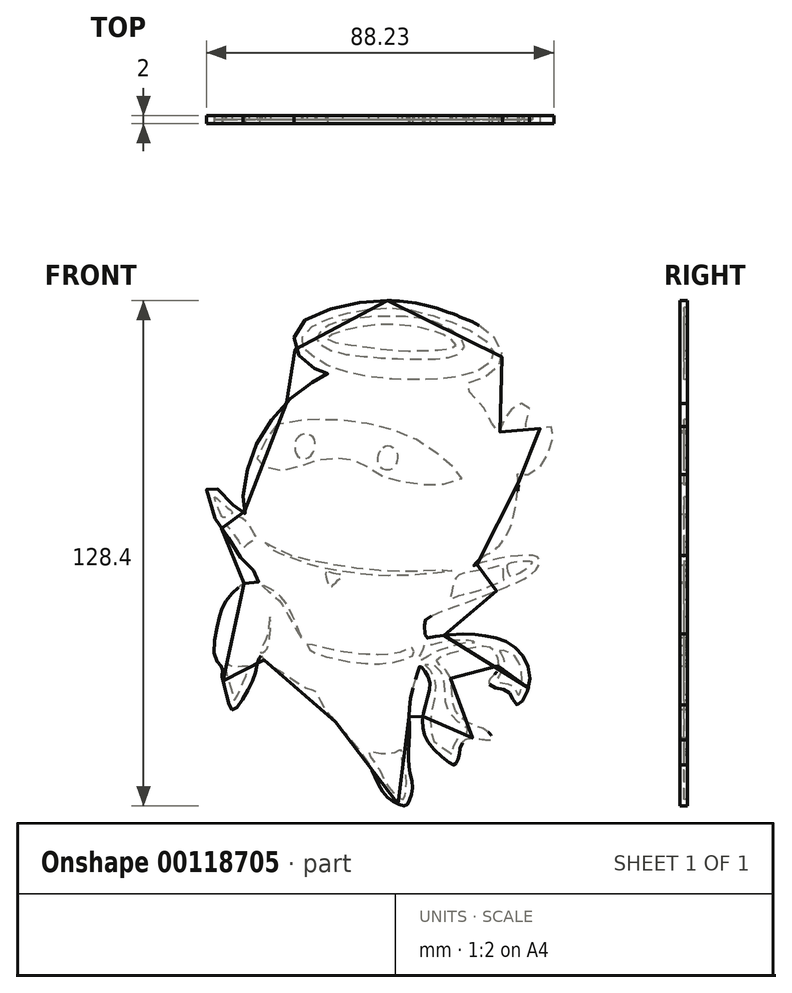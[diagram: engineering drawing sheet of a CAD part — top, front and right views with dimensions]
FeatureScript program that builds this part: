
annotation { "Feature Type Name" : "Feature", "Feature Type Description" : "" }
export const myFeature = defineFeature(function(context is Context, id is Id, definition is map)
    precondition{}
    {
        {
            var Q0;
            Q0=qCreatedBy(makeId("Front.planeOp"),FACE);
            var sketch = newSketch(context, id + "F0", { "sketchPlane" : qUnion([Q0])});
            skFitSpline(sketch, "E0", {"points": [v(2.08, 54.07) * mm, v(-5.17, 53.57) * mm, v(-13.1, 51.71) * mm, v(-19.17, 48.85) * mm, v(-21.36, 45.64) * mm, v(-21.53, 42.1) * mm, v(-19.68, 39.4) * mm, v(-16.64, 36.87) * mm, v(-13.94, 35.86) * mm, v(-13.1, 35.52) * mm, v(-13.6, 35.36) * mm, v(-16.98, 33.33) * mm, v(-22.04, 29.62) * mm, v(-27.1, 24.06) * mm, v(-31.14, 17.82) * mm, v(-33.33, 11.58) * mm, v(-34.52, 4.83) * mm, v(-34.52, 1.3) * mm, v(-34.18, -0.22) * mm, v(-35.02, 0.11) * mm, v(-38.23, 3.32) * mm, v(-41.26, 6.35) * mm, v(-43.45, 7.53) * mm, v(-43.28, 2.47) * mm, v(-39.74, -4.27) * mm, v(-37.55, -7.48) * mm, v(-34.85, -11.7) * mm, v(-33, -13.55) * mm, v(-30.64, -15.74) * mm, v(-30.47, -16.58) * mm, v(-30.97, -17.76) * mm, v(-33.17, -17.6) * mm, v(-35.36, -18.44) * mm, v(-39.07, -22.48) * mm, v(-40.92, -27.54) * mm, v(-41.6, -36.99) * mm, v(-39.91, -39) * mm, v(-39.91, -40.86) * mm, v(-38.73, -46.43) * mm, v(-37.21, -49.97) * mm, v(-34.18, -46.43) * mm, v(-31.48, -40.36) * mm, v(-30.64, -36.99) * mm, v(-30.13, -36.14) * mm, v(-29.12, -37.5) * mm, v(-24.73, -40.36) * mm, v(-18.66, -44.24) * mm, v(-16.13, -45.25) * mm, v(-15.63, -46.26) * mm, v(-13.94, -49.46) * mm, v(-12.09, -51.82) * mm, v(-9.39, -55.03) * mm, v(-6.19, -58.9) * mm, v(-3.15, -62.95) * mm, v(-1.3, -66.33) * mm, v(1.23, -71.22) * mm, v(4.6, -73.75) * mm, v(6.8, -74.25) * mm, v(7.64, -72.9) * mm, v(8.48, -69.7) * mm, v(7.64, -65.15) * mm, v(7.47, -60.26) * mm, v(7.64, -53.85) * mm, v(7.98, -46.77) * mm, v(10, -39.68) * mm, v(10.34, -38.84) * mm, v(11.69, -40.19) * mm, v(12.87, -43.56) * mm, v(11.69, -48.79) * mm, v(11.01, -54.02) * mm, v(12.87, -58.74) * mm, v(18.6, -63.8) * mm, v(19.28, -63.8) * mm, v(20.12, -62.28) * mm, v(20.63, -59.41) * mm, v(22.48, -57.22) * mm, v(27.2, -57.56) * mm, v(28.55, -57.22) * mm, v(27.7, -55.53) * mm, v(23.83, -53.68) * mm, v(19.61, -50.64) * mm, v(18.43, -44.74) * mm, v(17.25, -40.19) * mm, v(14.56, -37.32) * mm, v(18.77, -35.3) * mm, v(24.17, -33.95) * mm, v(28.21, -33.95) * mm, v(30.07, -36.82) * mm, v(29.73, -40.36) * mm, v(28.05, -42.21) * mm, v(28.05, -43.56) * mm, v(30.57, -44.57) * mm, v(32.77, -45.25) * mm, v(33.95, -47.27) * mm, v(35.13, -48.62) * mm, v(37.32, -46.1) * mm, v(38, -39.52) * mm, v(34.96, -34.46) * mm, v(30.57, -31.93) * mm, v(25.68, -30.92) * mm, v(19.28, -30.75) * mm, v(12.53, -31.59) * mm, v(11.86, -31.59) * mm, v(11.52, -28.9) * mm, v(11.69, -27.2) * mm, v(13.54, -25.86) * mm, v(21.97, -22.65) * mm, v(33.95, -17.93) * mm, v(40.02, -14.22) * mm, v(40.7, -11.52) * mm, v(38.84, -10.68) * mm, v(31.08, -11.35) * mm, v(24.5, -13.04) * mm, v(24, -13.2) * mm, v(26.7, -10.68) * mm, v(28.38, -10) * mm, v(30.74, -7.81) * mm, v(33.44, -3.1) * mm, v(35.13, 5.34) * mm, v(35.3, 9.72) * mm, v(35.13, 10.06) * mm, v(38.16, 9.9) * mm, v(41.54, 12.76) * mm, v(43.73, 17.48) * mm, v(44.23, 21.53) * mm, v(43.22, 22.03) * mm, v(39.34, 21.2) * mm, v(36.81, 21.2) * mm, v(37.32, 22.88) * mm, v(38, 27.1) * mm, v(36.3, 27.94) * mm, v(33.95, 26.76) * mm, v(31.92, 24.4) * mm, v(30.4, 20.52) * mm, v(29.06, 22.03) * mm, v(26.36, 27.1) * mm, v(21.97, 32.49) * mm, v(24.84, 33.84) * mm, v(30.4, 37.55) * mm, v(31.08, 41.26) * mm, v(27.7, 46.15) * mm, v(19.95, 50.2) * mm, v(11.01, 53.06) * mm, v(2.08, 54.07) * mm]});
            skFitSpline(sketch, "E1", {"points": [v(-25.98, 22.59) * mm, v(-28.54, 19.18) * mm, v(-31.1, 13.4) * mm, v(-30.24, 12.46) * mm, v(-26.55, 11.04) * mm, v(-21.54, 11.52) * mm, v(-16.9, 13.31) * mm, v(-10.84, 14.07) * mm, v(-7.53, 13.88) * mm, v(-3.55, 12.27) * mm, v(-0.34, 10) * mm, v(5.34, 8.2) * mm, v(12.44, 7.26) * mm, v(17.27, 7.64) * mm, v(21.24, 9.24) * mm, v(18.78, 11.7) * mm, v(13.3, 16.34) * mm, v(4.68, 20.8) * mm, v(-4.5, 23.06) * mm, v(-12.64, 23.82) * mm, v(-17.47, 23.72) * mm, v(-25.98, 22.59) * mm]});
            skFitSpline(sketch, "E2", {"points": [v(-19.08, 20.13) * mm, v(-20.78, 19.18) * mm, v(-21.35, 17.95) * mm, v(-21.35, 15.68) * mm, v(-20.3, 14.26) * mm, v(-18.6, 13.98) * mm, v(-16.8, 15.5) * mm, v(-16.33, 17.95) * mm, v(-17, 19.56) * mm, v(-19.08, 20.13) * mm]});
            skFitSpline(sketch, "E3", {"points": [v(0.99, 16.72) * mm, v(2.12, 17.29) * mm, v(3.64, 16.72) * mm, v(4.58, 15.3) * mm, v(4.49, 13.4) * mm, v(3.64, 11.52) * mm, v(2.12, 11.04) * mm, v(0.14, 11.8) * mm, v(-0.34, 13.7) * mm, v(0.04, 15.5) * mm, v(0.99, 16.72) * mm]});
            skFitSpline(sketch, "E4", {"points": [v(-19.36, 42.1) * mm, v(-19.68, 44.24) * mm, v(-18, 46.87) * mm, v(-12.36, 49.65) * mm, v(-5.83, 51.32) * mm, v(2.2, 52.28) * mm, v(11.6, 50.85) * mm, v(19, 48.38) * mm, v(25.53, 45.04) * mm, v(28.7, 41.85) * mm, v(28.95, 40.1) * mm, v(27.67, 37.64) * mm, v(21.39, 35.01) * mm, v(14.38, 34.14) * mm, v(4.52, 34.06) * mm, v(-4.95, 35.17) * mm, v(-13.55, 37.8) * mm, v(-17.93, 40.74) * mm, v(-19.36, 42.1) * mm]});
            skFitSpline(sketch, "E5", {"points": [v(-14.66, 42.8) * mm, v(-11.32, 41.06) * mm, v(-2.96, 39.79) * mm, v(4.91, 39.3) * mm, v(14.78, 39.3) * mm, v(18.84, 39.94) * mm, v(21.23, 41.38) * mm, v(21.55, 43.53) * mm, v(18.52, 46.4) * mm, v(12.63, 49.18) * mm, v(4.6, 50.05) * mm, v(-4.24, 49.81) * mm, v(-9.97, 48.86) * mm, v(-13.55, 47.43) * mm, v(-15.78, 44.96) * mm, v(-15.86, 44.08) * mm, v(-14.66, 42.8) * mm]});
            skFitSpline(sketch, "E6", {"points": [v(-13.15, 44.32) * mm, v(-5.2, 42.57) * mm, v(4.36, 41.38) * mm, v(14.54, 41.54) * mm, v(19.48, 42.57) * mm, v(18.2, 44.32) * mm, v(13.59, 46.4) * mm, v(6.98, 47.74) * mm, v(0.22, 47.98) * mm, v(-5.35, 47.27) * mm, v(-11.32, 45.75) * mm, v(-13.15, 44.32) * mm]});
            skFitSpline(sketch, "E7", {"points": [v(-39.65, -1.04) * mm, v(-40.69, 0.87) * mm, v(-41.8, 4.13) * mm, v(-39.17, 1.9) * mm, v(-37.34, 0.31) * mm, v(-38.23, -0.56) * mm, v(-39.65, -1.04) * mm]});
            skFitSpline(sketch, "E8", {"points": [v(-34.4, -8.68) * mm, v(-33.2, -7.49) * mm, v(-31.14, -6.45) * mm, v(-31.53, -5.58) * mm, v(-32.89, -3.27) * mm, v(-35.83, -0.88) * mm, v(-37.42, -2.15) * mm, v(-38.94, -2.71) * mm, v(-37.42, -4.54) * mm, v(-34.4, -8.68) * mm]});
            skFitSpline(sketch, "E9", {"points": [v(-13.55, -14.89) * mm, v(-12.67, -18.7) * mm, v(-12.28, -18.7) * mm, v(-9.65, -16.16) * mm, v(-9.33, -15.68) * mm, v(-11.96, -15.13) * mm, v(-13.55, -14.89) * mm]});
            skFitSpline(sketch, "E10", {"points": [v(-28.99, -7.33) * mm, v(-25.49, -9.32) * mm, v(-15.78, -12.18) * mm, v(-2.09, -14.25) * mm, v(10, -14.57) * mm, v(18.2, -14.4) * mm, v(18.52, -14.57) * mm, v(15.18, -15.05) * mm, v(6.74, -15.76) * mm, v(-1.13, -15.68) * mm, v(-8.46, -14.89) * mm, v(-15.38, -13.61) * mm, v(-20.95, -11.86) * mm, v(-25.8, -9.95) * mm, v(-27.95, -8.68) * mm, v(-28.99, -7.33) * mm]});
            skFitSpline(sketch, "E11", {"points": [v(21.63, -15.13) * mm, v(19.48, -16.32) * mm, v(18.52, -19.18) * mm, v(18.04, -21.5) * mm, v(17.97, -21.97) * mm, v(20.11, -20.86) * mm, v(23.14, -20.22) * mm, v(31.65, -16.88) * mm, v(31.65, -16.64) * mm, v(31.26, -13.22) * mm, v(29.82, -13.53) * mm, v(21.63, -15.13) * mm]});
            skFitSpline(sketch, "E12", {"points": [v(32.45, -13.22) * mm, v(33, -15.6) * mm, v(33.64, -16) * mm, v(37.94, -13.53) * mm, v(38.9, -12.42) * mm, v(38.18, -12.18) * mm, v(34.6, -12.42) * mm, v(32.45, -13.22) * mm]});
            skFitSpline(sketch, "E13", {"points": [v(-29.78, -18.3) * mm, v(-26.44, -21.17) * mm, v(-23.18, -25.71) * mm, v(-19.84, -31.76) * mm, v(-19.52, -32.24) * mm, v(-21.75, -26.59) * mm, v(-26.28, -19.98) * mm, v(-29.78, -18.3) * mm]});
            skFitSpline(sketch, "E14", {"points": [v(-39.1, -38.36) * mm, v(-37.1, -46.56) * mm, v(-36.79, -47.44) * mm, v(-33.29, -39.8) * mm, v(-33.29, -38.92) * mm, v(-36.3, -39) * mm, v(-38.06, -38.6) * mm, v(-39.1, -38.36) * mm]});
            skFitSpline(sketch, "E15", {"points": [v(-18.32, -33.35) * mm, v(-17.29, -34.86) * mm, v(-13.79, -36.3) * mm, v(-6.07, -37.89) * mm, v(2.77, -37.97) * mm, v(8.26, -36.3) * mm, v(8.73, -35.42) * mm, v(8.65, -34.3) * mm, v(7.38, -34.38) * mm, v(5.55, -35.26) * mm, v(0.14, -35.9) * mm, v(-6.47, -35.58) * mm, v(-11.96, -34.62) * mm, v(-17.13, -33.35) * mm, v(-18.32, -33.35) * mm]});
            skFitSpline(sketch, "E16", {"points": [v(11.36, -33.59) * mm, v(10.88, -35.02) * mm, v(9.93, -36.77) * mm, v(10.17, -37.33) * mm, v(13.75, -35.42) * mm, v(17.97, -33.9) * mm, v(22.18, -32.8) * mm, v(24.1, -32.8) * mm, v(24.33, -32.63) * mm, v(22.42, -32.32) * mm, v(17.33, -32.47) * mm, v(12.4, -33.5) * mm, v(11.36, -33.59) * mm]});
            skFitSpline(sketch, "E17", {"points": [v(-27.8, -26.35) * mm, v(-28.2, -29.85) * mm, v(-28.99, -32.32) * mm, v(-30.13, -35.34) * mm, v(-29.07, -35.02) * mm, v(-27.95, -32.47) * mm, v(-27.64, -27.54) * mm, v(-27.8, -26.35) * mm]});
            skFitSpline(sketch, "E18", {"points": [v(11.68, -38.44) * mm, v(12.63, -39.56) * mm, v(13.9, -41.63) * mm, v(14.3, -44.57) * mm, v(13.43, -49.9) * mm, v(12.95, -53.17) * mm, v(13.67, -57.46) * mm, v(14.94, -58.82) * mm, v(17.8, -60.73) * mm, v(18.44, -61.44) * mm, v(18.84, -59.45) * mm, v(19.88, -57.14) * mm, v(22.5, -55.71) * mm, v(22.58, -54.92) * mm, v(19.16, -52.3) * mm, v(16.93, -48.4) * mm, v(16.61, -43.7) * mm, v(16.13, -41.23) * mm, v(14.15, -38.6) * mm, v(11.68, -38.44) * mm]});
            skFitSpline(sketch, "E19", {"points": [v(30.54, -34.94) * mm, v(31.33, -36.21) * mm, v(31.26, -39.8) * mm, v(29.82, -42.34) * mm, v(30.3, -42.82) * mm, v(32.85, -43.38) * mm, v(34.6, -44.73) * mm, v(35.31, -46.16) * mm, v(35.71, -45.69) * mm, v(36.27, -41.87) * mm, v(35.71, -38.6) * mm, v(33.4, -35.5) * mm, v(30.54, -34.94) * mm]});
            skFitSpline(sketch, "E20", {"points": [v(-2.65, -60.73) * mm, v(-0.66, -63.99) * mm, v(1.01, -67.17) * mm, v(3.56, -71) * mm, v(5.95, -72.66) * mm, v(6.66, -71) * mm, v(6.82, -66.85) * mm, v(5.79, -63.11) * mm, v(5.55, -60) * mm, v(4.28, -60.65) * mm, v(0.7, -61.12) * mm, v(-2.65, -60.73) * mm]});
            skSolve(sketch);
        }
        {
            var Q0;
            Q0=makeQuery(id+"F0.imprint","IMPRINT",FACE,{"disambiguationData":[TD([[makeQuery(id+"F0.imprint","IMPRINT",EDGE,{"derivedFrom":sQuery(id+"F0.wireOp",EDGE,"E5")}),1.0]])]});
            var Q1;
            Q1=makeQuery(id+"F0.imprint","IMPRINT",FACE,{"disambiguationData":[TD([[makeQuery(id+"F0.imprint","IMPRINT",EDGE,{"derivedFrom":sQuery(id+"F0.wireOp",EDGE,"E0")}),1.0]])]});
            var Q2;
            Q2=makeQuery(id+"F0.imprint","IMPRINT",FACE,{"disambiguationData":[TD([[makeQuery(id+"F0.imprint","IMPRINT",EDGE,{"derivedFrom":sQuery(id+"F0.wireOp",EDGE,"E2")}),1.0]])]});
            var Q3;
            Q3=makeQuery(id+"F0.imprint","IMPRINT",FACE,{"disambiguationData":[TD([[makeQuery(id+"F0.imprint","IMPRINT",EDGE,{"derivedFrom":sQuery(id+"F0.wireOp",EDGE,"E3")}),-1.0]])]});
            extrude(context, id + "F1", {"entities" : qUnion([Q0, Q1, Q2, Q3]), "oppositeDirection" : true, "depth" : 1 * mm});
        }
        {
            var Q0;
            Q0=makeQuery(id+"F0.imprint","IMPRINT",FACE,{"disambiguationData":[TD([[makeQuery(id+"F0.imprint","IMPRINT",EDGE,{"derivedFrom":sQuery(id+"F0.wireOp",EDGE,"E4")}),-1.0]])]});
            var Q1;
            Q1=makeQuery(id+"F0.imprint","IMPRINT",FACE,{"disambiguationData":[TD([[makeQuery(id+"F0.imprint","IMPRINT",EDGE,{"derivedFrom":sQuery(id+"F0.wireOp",EDGE,"E15")}),1.0]])]});
            var Q2;
            Q2=makeQuery(id+"F0.imprint","IMPRINT",FACE,{"disambiguationData":[TD([[makeQuery(id+"F0.imprint","IMPRINT",EDGE,{"derivedFrom":sQuery(id+"F0.wireOp",EDGE,"E11")}),1.0]])]});
            var Q3;
            Q3=makeQuery(id+"F0.imprint","IMPRINT",FACE,{"disambiguationData":[TD([[makeQuery(id+"F0.imprint","IMPRINT",EDGE,{"derivedFrom":sQuery(id+"F0.wireOp",EDGE,"E6")}),1.0]])]});
            var Q4;
            Q4=makeQuery(id+"F0.imprint","IMPRINT",FACE,{"disambiguationData":[TD([[makeQuery(id+"F0.imprint","IMPRINT",EDGE,{"derivedFrom":sQuery(id+"F0.wireOp",EDGE,"E0")}),1.0]])]});
            var Q5;
            Q5=makeQuery(id+"F0.imprint","IMPRINT",FACE,{"disambiguationData":[TD([[makeQuery(id+"F0.imprint","IMPRINT",EDGE,{"derivedFrom":sQuery(id+"F0.wireOp",EDGE,"E18")}),1.0]])]});
            var Q6;
            Q6=makeQuery(id+"F0.imprint","IMPRINT",FACE,{"disambiguationData":[TD([[makeQuery(id+"F0.imprint","IMPRINT",EDGE,{"derivedFrom":sQuery(id+"F0.wireOp",EDGE,"E20")}),1.0]])]});
            var Q7;
            Q7=makeQuery(id+"F0.imprint","IMPRINT",FACE,{"disambiguationData":[TD([[makeQuery(id+"F0.imprint","IMPRINT",EDGE,{"derivedFrom":sQuery(id+"F0.wireOp",EDGE,"E1")}),1.0]])]});
            var Q8;
            Q8=makeQuery(id+"F0.imprint","IMPRINT",FACE,{"disambiguationData":[TD([[makeQuery(id+"F0.imprint","IMPRINT",EDGE,{"derivedFrom":sQuery(id+"F0.wireOp",EDGE,"E10")}),-1.0]])]});
            var Q9;
            Q9=makeQuery(id+"F0.imprint","IMPRINT",FACE,{"disambiguationData":[TD([[makeQuery(id+"F0.imprint","IMPRINT",EDGE,{"derivedFrom":sQuery(id+"F0.wireOp",EDGE,"E14")}),1.0]])]});
            var Q10;
            Q10=makeQuery(id+"F0.imprint","IMPRINT",FACE,{"disambiguationData":[TD([[makeQuery(id+"F0.imprint","IMPRINT",EDGE,{"derivedFrom":sQuery(id+"F0.wireOp",EDGE,"E5")}),1.0]])]});
            var Q11;
            Q11=makeQuery(id+"F0.imprint","IMPRINT",FACE,{"disambiguationData":[TD([[makeQuery(id+"F0.imprint","IMPRINT",EDGE,{"derivedFrom":sQuery(id+"F0.wireOp",EDGE,"E13")}),1.0]])]});
            var Q12;
            Q12=makeQuery(id+"F0.imprint","IMPRINT",FACE,{"disambiguationData":[TD([[makeQuery(id+"F0.imprint","IMPRINT",EDGE,{"derivedFrom":sQuery(id+"F0.wireOp",EDGE,"E8")}),1.0]])]});
            var Q13;
            Q13=makeQuery(id+"F0.imprint","IMPRINT",FACE,{"disambiguationData":[TD([[makeQuery(id+"F0.imprint","IMPRINT",EDGE,{"derivedFrom":sQuery(id+"F0.wireOp",EDGE,"E2")}),1.0]])]});
            var Q14;
            Q14=makeQuery(id+"F0.imprint","IMPRINT",FACE,{"disambiguationData":[TD([[makeQuery(id+"F0.imprint","IMPRINT",EDGE,{"derivedFrom":sQuery(id+"F0.wireOp",EDGE,"E19")}),1.0]])]});
            var Q15;
            Q15=makeQuery(id+"F0.imprint","IMPRINT",FACE,{"disambiguationData":[TD([[makeQuery(id+"F0.imprint","IMPRINT",EDGE,{"derivedFrom":sQuery(id+"F0.wireOp",EDGE,"E3")}),-1.0]])]});
            var Q16;
            Q16=makeQuery(id+"F0.imprint","IMPRINT",FACE,{"disambiguationData":[TD([[makeQuery(id+"F0.imprint","IMPRINT",EDGE,{"derivedFrom":sQuery(id+"F0.wireOp",EDGE,"E7")}),-1.0]])]});
            var Q17;
            Q17=makeQuery(id+"F0.imprint","IMPRINT",FACE,{"disambiguationData":[TD([[makeQuery(id+"F0.imprint","IMPRINT",EDGE,{"derivedFrom":sQuery(id+"F0.wireOp",EDGE,"E12")}),1.0]])]});
            var Q18;
            Q18=makeQuery(id+"F0.imprint","IMPRINT",FACE,{"disambiguationData":[TD([[makeQuery(id+"F0.imprint","IMPRINT",EDGE,{"derivedFrom":sQuery(id+"F0.wireOp",EDGE,"E16")}),1.0]])]});
            var Q19;
            Q19=makeQuery(id+"F0.imprint","IMPRINT",FACE,{"disambiguationData":[TD([[makeQuery(id+"F0.imprint","IMPRINT",EDGE,{"derivedFrom":sQuery(id+"F0.wireOp",EDGE,"E17")}),1.0]])]});
            var Q20;
            Q20=makeQuery(id+"F0.imprint","IMPRINT",FACE,{"disambiguationData":[TD([[makeQuery(id+"F0.imprint","IMPRINT",EDGE,{"derivedFrom":sQuery(id+"F0.wireOp",EDGE,"E9")}),1.0]])]});
            extrude(context, id + "F2", {"entities" : qUnion([Q0, Q1, Q2, Q3, Q4, Q5, Q6, Q7, Q8, Q9, Q10, Q11, Q12, Q13, Q14, Q15, Q16, Q17, Q18, Q19, Q20]), "operationType" : NewBodyOperationType.ADD, "depth" : 1 * mm});
        }
    });
